# Revit family: Ctrl_AMTU31_Indoor Unit
name_source: partatom
category: Mechanical Equipment
revit_build: Autodesk Revit 2017 (Build: 20160225_1515(x64)
units: mm (PartAtom-declared; Revit-internal decimal feet)

## family parameters
Always vertical = Yes
Cut with Voids When Loaded = No
OmniClass Number = 23.75.00.00
OmniClass Title = Climate Control (HVAC)
Part Type = Normal
Room Calculation Point = No
Round Connector Dimension = Use Diameter
Shared = No
Work Plane-Based = No

## types (1)
- RBC-AMTU31
    Airflow (m3/h) = -
    Article Description = Control
    Article Type = RBC-AMTU31
    Capacities - Cooling (kW) = -
    Capacities - Heating (kW) = -
    Capacity = -
    Compressor detail - Motor output  (kW) = -
    Compressor detail - Type = -
    Content Supplier URL = www.hcltech.com
    Depth (mm) = 16 mm  [stored 0.0524934 ft]
    Description = Control
    EMCS = 4
    ETIM Article Class = EC001213
    Energy Class = -
    Frequency (Hz) = -
    Height (mm) = 120 mm  [stored 0.393701 ft]
    MCA (A) = -
    MEPcontent Class = HEATPUMP
    MOCP (A) = -
    Manufacturer = Toshiba
    Manufacturer Art. No. = RBC-AMTU31
    Manufacturer URL = https://www.toshiba-carrier.co.jp
    Model = RBC-AMTU31
    Operating range - Cooling (°C) = -
    Operating range - Heating (°C) = -
    Part load = -
    Power consumption-Cooling (Kw) = -
    Power consumption-Heating (Kw) = -
    Rated efficiency - EER / COP = -
    Red = RGB COLOR 255 000 000
    Refrigerant Information = -
    Revit Version = 2017
    Running current-Cooling (A) = -
    Running current-Heating (A) = -
    Seasonal & Rated efficiency = -
    Sound pressure - Cooling (dB) = -
    Sound pressure - Heating (dB) = -
    Sound pressure - High (dB) = -
    Sound pressure - Low (dB) = -
    Sound pressure - Mid (dB) = -
    Starting current (A) = -
    Static pressure (Pa) = -
    URL = https://www.toshiba-carrier.co.jp
    Voltage (V) = -
    Weight (Kg) = -
    White = RGB COLOR 255 255 255
    Width (mm) = 120 mm  [stored 0.393701 ft]

note: [stored X ft] marks values corroborated as IEEE doubles in the binary element streams (Revit-internal decimal feet)

## geometry (parser evidence)
native form markers: Sweep x2
no freeform markers — native parametric forms only
